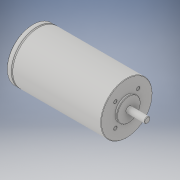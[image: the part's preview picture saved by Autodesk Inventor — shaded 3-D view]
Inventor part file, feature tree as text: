
AUTODESK INVENTOR PART (.ipt)
format: ipt  version: 2018 (Build 220112000, 112)  size: 203,264 bytes
history: native  units: in
note: dims shown in document units (in); Inventor stores cm internally (conversion verified against a paired STEP export)
features: extrude x1, sketch x1, imported_body x1
ambient origin geometry x8: Origin, YZ Plane, XZ Plane, XY Plane, X Axis, Y Axis, Z Axis, Center Point
bodies: Solid1 (feature_tree)
feature tree (3):
  extrude  "Extrusion1"  [1 undecoded]
  sketch  "Sketch1"  dims[d0=0.3937in d1=0.0in]
  imported_body  "Base1"
note: 1 required parameter value undecoded (feature->parameter linkage not recoverable at this tier; creation-order binding heuristic only, values carry confidence <= 0.55)
